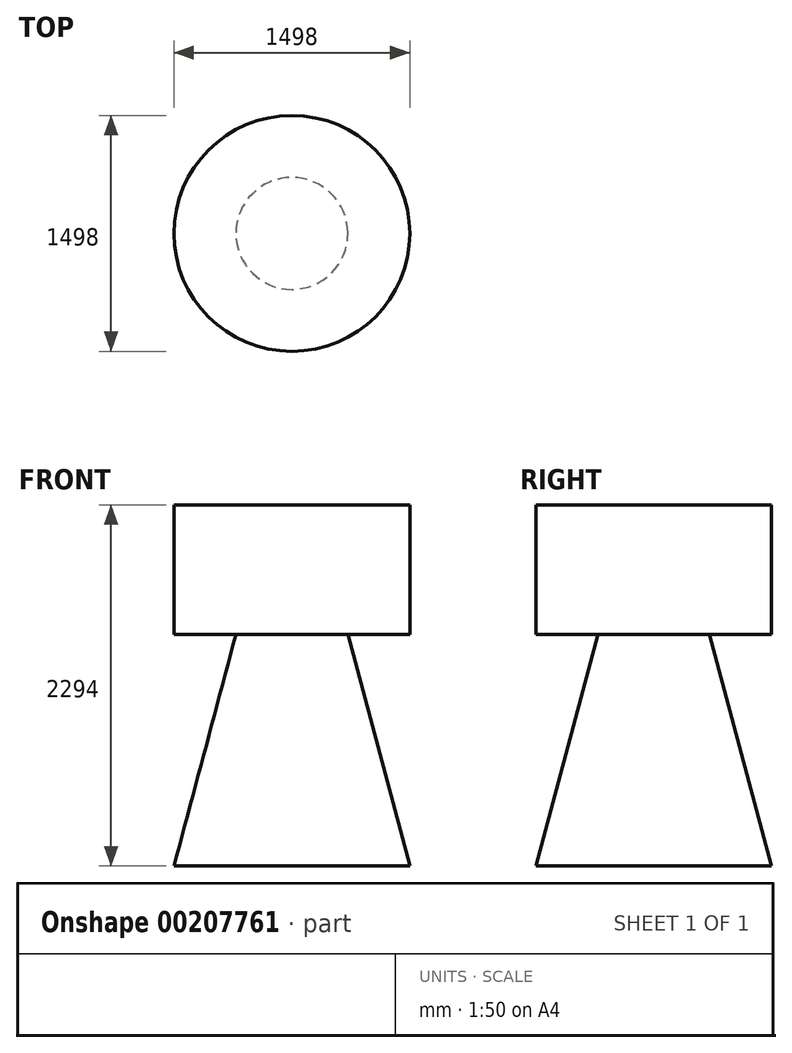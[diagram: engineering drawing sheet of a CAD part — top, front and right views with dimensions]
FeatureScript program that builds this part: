
annotation { "Feature Type Name" : "Feature", "Feature Type Description" : "" }
export const myFeature = defineFeature(function(context is Context, id is Id, definition is map)
    precondition{}
    {
        {
            var Q0;
            Q0=qCreatedBy(makeId("Front.planeOp"),FACE);
            var sketch = newSketch(context, id + "F0", { "sketchPlane" : qUnion([Q0])});
            skLineSegment(sketch, "E0", {"start": v(0, 2294) * mm, "end": v(749, 2294) * mm});
            skLineSegment(sketch, "E1", {"start": v(749, 2294) * mm, "end": v(749, 1471) * mm});
            skLineSegment(sketch, "E2", {"start": v(749, 1471) * mm, "end": v(355.5, 1471) * mm});
            skLineSegment(sketch, "E3", {"start": v(355.5, 1471) * mm, "end": v(749, 0) * mm});
            skLineSegment(sketch, "E4", {"start": v(749, 0) * mm, "end": v(0, 0) * mm});
            skLineSegment(sketch, "E5", {"start": v(0, 0) * mm, "end": v(0, 2294) * mm});
            skLineSegment(sketch, "E6", {"start": v(0, 0) * mm, "end": v(0, 95.7) * mm, "construction": true});
            skSolve(sketch);
        }
        {
            var Q0;
            Q0=makeQuery(id+"F0.imprint","IMPRINT",FACE,{"disambiguationData":[TD([[makeQuery(id+"F0.imprint","IMPRINT",EDGE,{"derivedFrom":sQuery(id+"F0.wireOp",EDGE,"E0")}),-1.0]])]});
            var Q1;
            Q1=sQuery(id+"F0.wireOp",EDGE,"E5");
            revolve(context, id + "F1", {"entities" : qUnion([Q0]), "axis" : qUnion([Q1]), "revolveType" : RevolveType.FULL});
        }
    });
